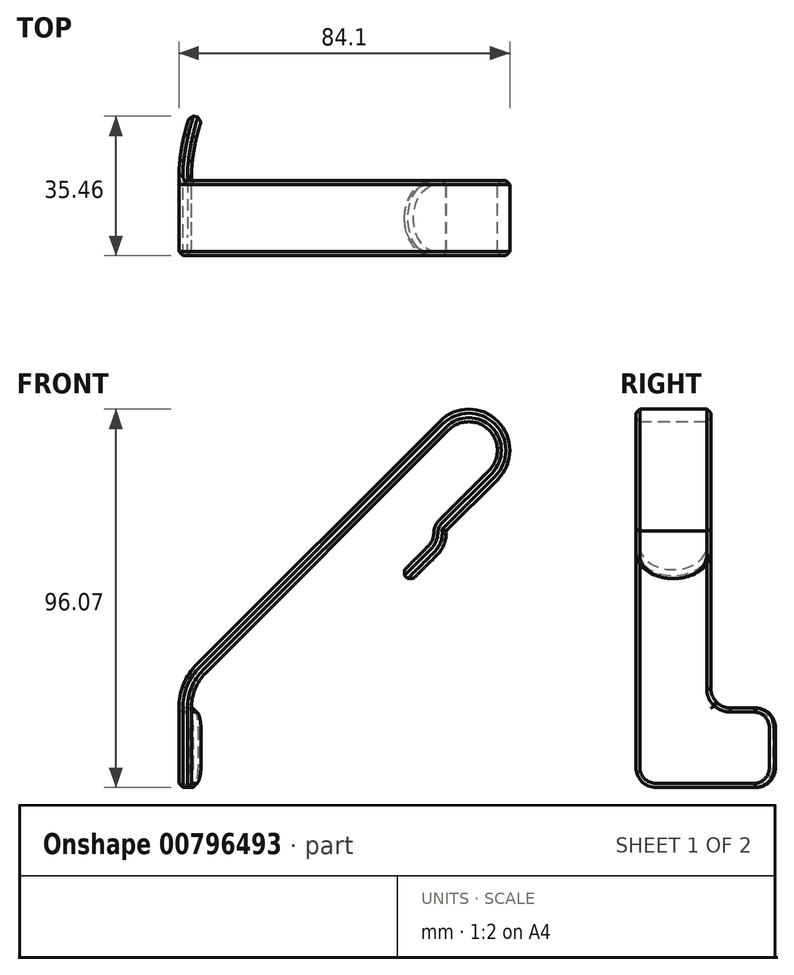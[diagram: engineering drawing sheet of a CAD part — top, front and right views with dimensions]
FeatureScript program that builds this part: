
annotation { "Feature Type Name" : "Feature", "Feature Type Description" : "" }
export const myFeature = defineFeature(function(context is Context, id is Id, definition is map)
    precondition{}
    {
        {
            var Q0;
            Q0=qCreatedBy(makeId("Front.planeOp"),FACE);
            var sketch = newSketch(context, id + "F0", { "sketchPlane" : qUnion([Q0])});
            skLineSegment(sketch, "E0", {"start": v(3.72, 3.72) * mm, "end": v(65.37, 65.37) * mm});
            skLineSegment(sketch, "E1", {"start": v(0, -5.26) * mm, "end": v(0, -25.4) * mm});
            skPoint(sketch, "E2.visualSharp", {"position": v(0, 0) * mm});
            skArc(sketch, "E2.filletArc", {"start": v(3.72, 3.72) * mm, "mid": v(0.97, -0.4) * mm, "end": v(0, -5.26) * mm});
            skLineSegment(sketch, "E3", {"start": v(70.5, 70.5) * mm, "end": v(80.75, 60.24) * mm, "construction": true});
            skLineSegment(sketch, "E4", {"start": v(75.62, 55.11) * mm, "end": v(62.99, 42.48) * mm});
            skLineSegment(sketch, "E5", {"start": v(60.2, 35.92) * mm, "end": v(53.45, 29.17) * mm});
            skArc(sketch, "E6", {"start": v(60.2, 35.92) * mm, "mid": v(61.21, 37.42) * mm, "end": v(61.6, 39.2) * mm});
            skArc(sketch, "E7", {"start": v(62.99, 42.48) * mm, "mid": v(61.97, 40.97) * mm, "end": v(61.6, 39.2) * mm});
            skArc(sketch, "E8", {"start": v(75.62, 55.11) * mm, "mid": v(75.62, 65.37) * mm, "end": v(65.37, 65.37) * mm});
            skLineSegment(sketch, "E9", {"start": v(62.99, 42.48) * mm, "end": v(52.73, 52.73) * mm, "construction": true});
            skLineSegment(sketch, "E10", {"start": v(53.45, 29.17) * mm, "end": v(41.3, 41.3) * mm, "construction": true});
            skLineSegment(sketch, "E11.0", {"start": v(62.44, 33.67) * mm, "end": v(55.7, 26.92) * mm});
            skArc(sketch, "E11.1", {"start": v(62.44, 33.67) * mm, "mid": v(64.25, 36.47) * mm, "end": v(64.76, 39.75) * mm});
            skLineSegment(sketch, "E11.2", {"start": v(77.87, 52.87) * mm, "end": v(64.76, 39.75) * mm});
            skLineSegment(sketch, "E11.3", {"start": v(-3.17, -5.26) * mm, "end": v(-3.17, -25.4) * mm});
            skArc(sketch, "E11.4", {"start": v(1.47, 5.96) * mm, "mid": v(-1.97, 0.81) * mm, "end": v(-3.17, -5.26) * mm});
            skLineSegment(sketch, "E11.5", {"start": v(1.47, 5.96) * mm, "end": v(63.12, 67.61) * mm});
            skArc(sketch, "E11.6", {"start": v(77.87, 52.87) * mm, "mid": v(77.87, 67.61) * mm, "end": v(63.12, 67.61) * mm});
            skLineSegment(sketch, "E12", {"start": v(0, -25.4) * mm, "end": v(-3.17, -25.4) * mm});
            skLineSegment(sketch, "E13", {"start": v(53.45, 29.17) * mm, "end": v(55.7, 26.92) * mm});
            skSolve(sketch);
        }
        {
            var Q0;
            Q0 = qSketchRegion(id + "F0", true);
            extrude(context, id + "F1", {"entities" : qUnion([Q0]), "depth" : 19.05 * mm, "offsetDistance" : 25.4 * mm});
        }
        {
            var Q0;
            Q0=makeQuery(id+"F1.opExtrude","SWEPT_FACE",FACE,{"disambiguationData":[OSD([sQuery(id+"F0.wireOp",EDGE,"E12")])]});
            var sketch = newSketch(context, id + "F2", { "sketchPlane" : qUnion([Q0])});
            skLineSegment(sketch, "E14.0", {"start": v(-3.17, 19.05) * mm, "end": v(-3.17, 0) * mm});
            skLineSegment(sketch, "E14.1", {"start": v(0, 0) * mm, "end": v(-3.17, 0) * mm, "construction": true});
            skLineSegment(sketch, "E14.2", {"start": v(0, 19.05) * mm, "end": v(0, 0) * mm});
            skLineSegment(sketch, "E15.0", {"start": v(0, 19.05) * mm, "end": v(-3.17, 19.05) * mm});
            skArc(sketch, "E16", {"start": v(0, 0) * mm, "mid": v(0.71, -8.12) * mm, "end": v(2.82, -16) * mm});
            skArc(sketch, "E17.0", {"start": v(-3.17, 0) * mm, "mid": v(-2.46, -8.4) * mm, "end": v(-0.35, -16.56) * mm});
            skLineSegment(sketch, "E18", {"start": v(2.82, -16) * mm, "end": v(-0.35, -16.56) * mm});
            skLineSegment(sketch, "E19", {"start": v(0, 0) * mm, "end": v(2.82, -16) * mm, "construction": true});
            skSolve(sketch);
        }
        {
            var Q0;
            Q0 = qSketchRegion(id + "F2", true);
            var Q1;
            Q1=makeQuery(id+"F1.opExtrude","CAP_VERTEX",VERTEX,{"disambiguationData":[OSD([sQuery(id+"F0.wireOp",EDGE,"E11.3"),sQuery(id+"F0.wireOp",EDGE,"E11.4")])],"isStart":true});
            extrude(context, id + "F3", {"entities" : qUnion([Q0]), "operationType" : NewBodyOperationType.ADD, "endBound" : BoundingType.UP_TO_VERTEX, "oppositeDirection" : true, "depth" : 25.4 * mm, "endBoundEntityVertex" : qUnion([Q1]), "offsetDistance" : 25.4 * mm});
        }
        {
            var Q0;
            Q0=makeQuery(id+"F1.opExtrude","CAP_EDGE",EDGE,{"disambiguationData":[OSD([sQuery(id+"F0.wireOp",EDGE,"E12")])],"isStart":false});
            var Q1;
            Q1=makeQuery(id+"F3.opExtrude","CAP_EDGE",EDGE,{"disambiguationData":[OSD([sQuery(id+"F2.wireOp",EDGE,"E18")])],"isStart":true});
            var Q2;
            Q2=makeQuery(id+"F3.opExtrude","CAP_EDGE",EDGE,{"disambiguationData":[OSD([sQuery(id+"F2.wireOp",EDGE,"E18")])],"isStart":false});
            var Q3;
            Q3=makeQuery(id+"F3.boolean.opBoolean","INTERSECT",EDGE,{"derivedFrom":[makeQuery(id+"F1.opExtrude","CAP_FACE",FACE,{"disambiguationData":[OSD([sQuery(id+"F0.wireOp",EDGE,"E0"),sQuery(id+"F0.wireOp",EDGE,"E1"),sQuery(id+"F0.wireOp",EDGE,"E2.filletArc"),sQuery(id+"F0.wireOp",EDGE,"E4"),sQuery(id+"F0.wireOp",EDGE,"E5"),sQuery(id+"F0.wireOp",EDGE,"E6"),sQuery(id+"F0.wireOp",EDGE,"E7"),sQuery(id+"F0.wireOp",EDGE,"E8"),sQuery(id+"F0.wireOp",EDGE,"E11.0"),sQuery(id+"F0.wireOp",EDGE,"E11.1"),sQuery(id+"F0.wireOp",EDGE,"E11.2"),sQuery(id+"F0.wireOp",EDGE,"E11.3"),sQuery(id+"F0.wireOp",EDGE,"E11.4"),sQuery(id+"F0.wireOp",EDGE,"E11.5"),sQuery(id+"F0.wireOp",EDGE,"E11.6"),sQuery(id+"F0.wireOp",EDGE,"E12"),sQuery(id+"F0.wireOp",EDGE,"E13")])],"isStart":true}),makeQuery(id+"F3.opExtrude","CAP_FACE",FACE,{"disambiguationData":[OSD([sQuery(id+"F2.wireOp",EDGE,"E14.0"),sQuery(id+"F2.wireOp",EDGE,"E14.2"),sQuery(id+"F2.wireOp",EDGE,"E15.0"),sQuery(id+"F2.wireOp",EDGE,"E16"),sQuery(id+"F2.wireOp",EDGE,"E17.0"),sQuery(id+"F2.wireOp",EDGE,"E18")])],"isStart":false})]});
            fillet(context, id + "F4", {"entities" : qUnion([Q0, Q1, Q2, Q3]), "radius" : 5.08 * mm, "tangentPropagation" : true, "allowEdgeOverflow" : false});
        }
        {
            var Q0;
            Q0=makeQuery(id+"F1.opExtrude","CAP_EDGE",EDGE,{"disambiguationData":[OSD([sQuery(id+"F0.wireOp",EDGE,"E13")])],"isStart":true});
            var Q1;
            Q1=makeQuery(id+"F1.opExtrude","CAP_EDGE",EDGE,{"disambiguationData":[OSD([sQuery(id+"F0.wireOp",EDGE,"E13")])],"isStart":false});
            fillet(context, id + "F5", {"entities" : qUnion([Q0, Q1]), "radius" : 9.52 * mm, "tangentPropagation" : true, "allowEdgeOverflow" : false});
        }
        {
            var Q0;
            Q0=makeQuery(id+"F1.opExtrude","CAP_EDGE",EDGE,{"disambiguationData":[OSD([sQuery(id+"F0.wireOp",EDGE,"E11.5")])],"isStart":true});
            var Q1;
            Q1=makeQuery(id+"F1.opExtrude","CAP_EDGE",EDGE,{"disambiguationData":[OSD([sQuery(id+"F0.wireOp",EDGE,"E11.1")])],"isStart":true});
            var Q2;
            Q2=makeQuery(id+"F1.opExtrude","CAP_EDGE",EDGE,{"disambiguationData":[OSD([sQuery(id+"F0.wireOp",EDGE,"E11.5")])],"isStart":false});
            var Q3;
            Q3=makeQuery(id+"F1.opExtrude","CAP_EDGE",EDGE,{"disambiguationData":[OSD([sQuery(id+"F0.wireOp",EDGE,"E0")])],"isStart":true});
            chamfer(context, id + "F6", {"entities" : qUnion([Q0, Q1, Q2, Q3]), "width" : 1.02 * mm, "tangentPropagation" : true});
        }
    });
